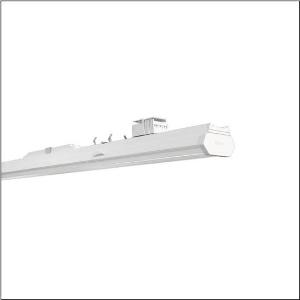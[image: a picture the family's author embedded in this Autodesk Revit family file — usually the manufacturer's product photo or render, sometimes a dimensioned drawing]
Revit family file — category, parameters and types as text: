
# Revit family: licross_r__11_protected_ho_51tp13cn4e5s_b79e
name_source: partatom
category: Lighting Fixtures
units: mm (PartAtom-declared; Revit-internal decimal feet)

## family parameters
Cut with Voids When Loaded = No
Host = Face
Light Source = No
Part Type = Normal
Room Calculation Point = No
Round Connector Dimension = Use Diameter
Shared = No

## types (1)
- --- (1 x LED, 14500 lm, 77.6 W, 4000K)
    Apparent Load = 78 VA
    CIE Flux Codes = 89 96 99 100 99
    Color Rendering = 80
    Color Temperature = 4000K
    Default Elevation = 1800 mm
    Description = Licross® 11 Protected HO, luminaire insert, of sheet steel, galvanised, coil coated, white, length: 1.500mm, width: 90mm, height: 101mm, LED rated luminous flux: 14.500lm, light colour: 840, control gear: ON/OFF Multilumen, CLOi, with plug, 3-pole, with phase selection, mains connection: 220..240V, AC, 50/60Hz, start of lifetime: 78W, end of service life: 87W, halogen-free wiring, primary light control with lens, of plastic, primary optical cover: cover, of PMMA, light emission: direct distribution, primary light characteristic: symmetric, protection rating (complete): IP64, insulation class (complete): insulation class I (protective earthing), certification: CE, ENEC, VDE, UKCA, protection symbol: D if used in an environment with conductive dust loads with corresponding accessories, impact resistance: IK06, permissible ambient temperature for indoor applications: -35..+35°C, corresponds to IFS (International Featured Standards) requirements for safety and quality in the food industry, reducing of maximum allowable ambient temperature of 5°C with ceiling mounting, LABS conformity tested according to VDMA 24364:2018-05, packaging unit: 1 piece
    Height = 92 mm
    Lamp = 1 x LED
    Lamp Light Flux = 14500 lm
    Lamp Power = 77.6 W
    Lamp count = 1
    Length = 1500 mm
    Luminous efficacy = 187 lm/W
    Manufacturer = Siteco
    ModVariant = No
    Model = 51TP13CN4E5S
    Mounting Place = Ceiling
    Mounting Type = Pendant
    Number of Poles = 1
    OnlyDefault = Yes
    Power Factor = 1
    Product Name = Licross® 11 Protected HO
    Product group = luminaire insert
    ProductGroupID = 901
    Protection Class = Protection class I
    Protection Degree = IP 64
    RLX_Detail_Level = 1
    RLX_Emergency_Light_Flux = 0 lm
    RLX_Emergency_Type = 0
    RLX_Emergency_Type_DB = No
    RlxData = <blob elided: 22033 chars, md5=1df86cdb>
    Socket = socket
    Standby Power = 0 W
    System Light Flux = 14500 lm
    System Power = 78 W
    Type Comments = factory setting: luminous flux: 100 % | (A | C | E) | 181 mA
    Type Image = l_1256148.jpg
    URL = http://relux.com
    VarID = @adj_037877
    Voltage = 0 V
    Weight = 0.00 kg
    Width = 88 mm

## geometry (parser evidence)
native form markers: Blend x4, Sweep x12
no freeform markers — native parametric forms only
